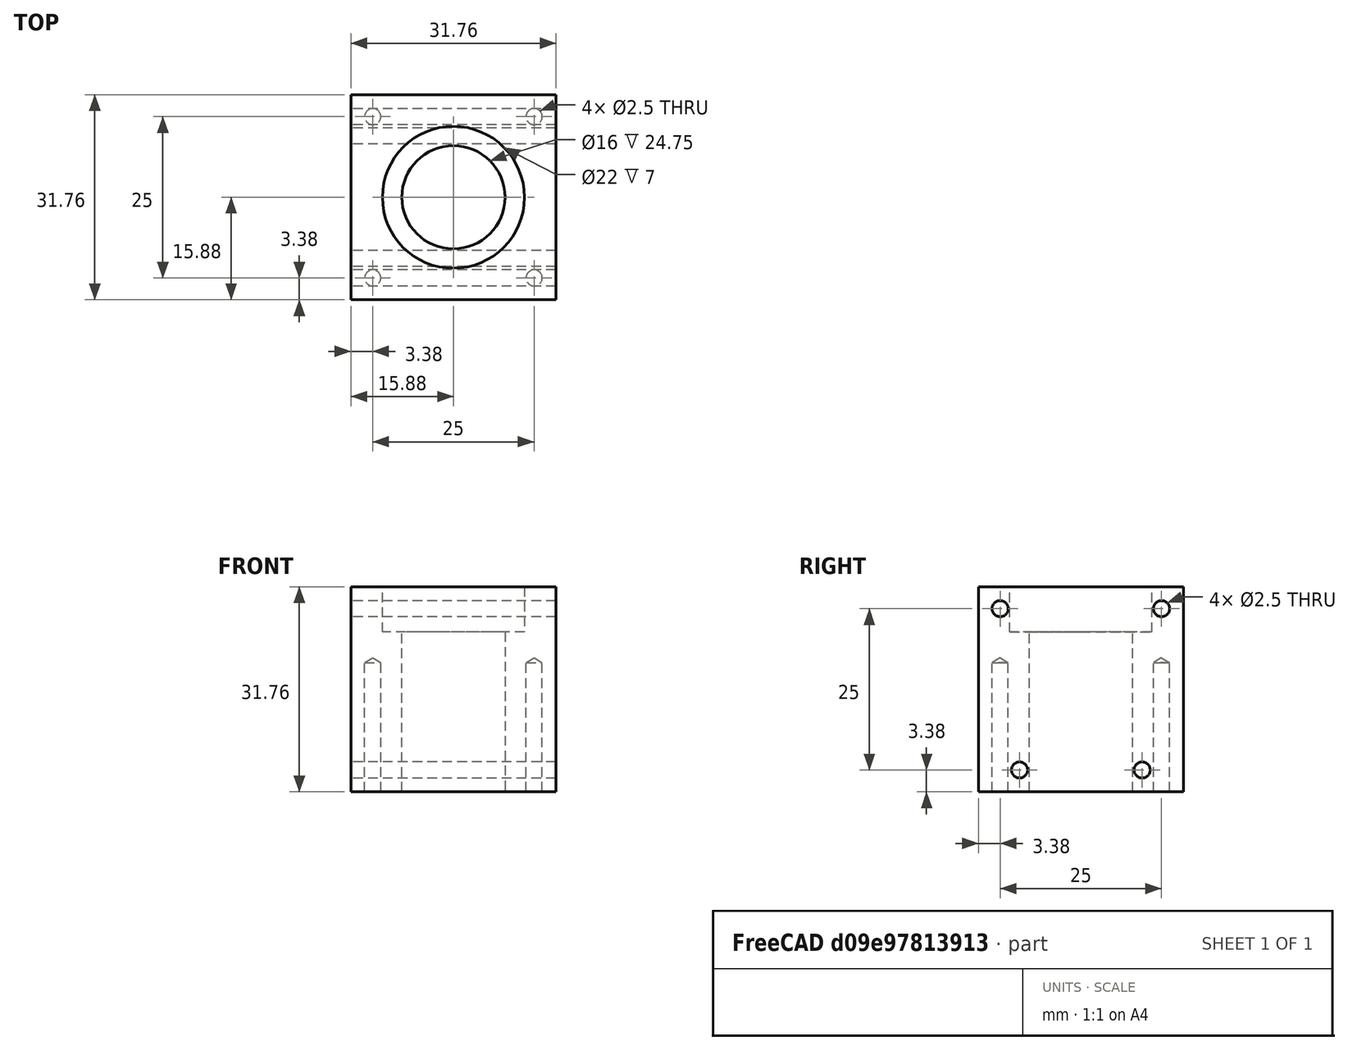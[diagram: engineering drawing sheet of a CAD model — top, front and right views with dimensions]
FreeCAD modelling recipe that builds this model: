
FCSTD DOCUMENT  (FreeCAD 0.21R33771 (Git))
Label: Upper Bearing Block
License: All rights reserved
LicenseURL: http://en.wikipedia.org/wiki/All_rights_reserved
objects: TechDraw::DrawViewDimension×8, Sketcher::SketchObject×5, TechDraw::DrawProjGroupItem×5, PartDesign::Pocket×2, PartDesign::Hole×2, TechDraw::DrawViewAnnotation×2, PartDesign::CoordinateSystem×2, TechDraw::DrawViewBalloon×2, PartDesign::Pad×1, TechDraw::DrawSVGTemplate×1, PartDesign::Body×1, TechDraw::DrawProjGroup×1, TechDraw::DrawPage×1
note: 18 computed .brp shape members not serialized (recipe doc carries the construction recipe); baked Part::Feature solids carry a one-line shape summary decoded from their .brp

FEATURE [Sketcher::SketchObject] Sketch
  FullyConstrained = true
  MapMode = 5
  Support = -> [XY_Plane]
  sketch-geometry (5):
    g0: LineSegment StartX=-15.875 StartY=-15.875 StartZ=0 EndX=-15.875 EndY=15.875 EndZ=0
    g1: LineSegment StartX=-15.875 StartY=15.875 StartZ=0 EndX=15.875 EndY=15.875 EndZ=0
    g2: LineSegment StartX=15.875 StartY=15.875 StartZ=0 EndX=15.875 EndY=-15.875 EndZ=0
    g3: LineSegment StartX=15.875 StartY=-15.875 StartZ=0 EndX=-15.875 EndY=-15.875 EndZ=0
    g4: GeomPoint X=0 Y=0 Z=0
  constraints (12):
    c: Coincident(g0,g1)
    c: Coincident(g1,g2)
    c: Coincident(g2,g3)
    c: Coincident(g3,g0)
    c: Horizontal(g1)
    c: Horizontal(g3)
    c: Vertical(g0)
    c: Vertical(g2)
    c: Symmetric(g1,g0,g4)
    c: Coincident(g4,g-1)
    c: DistanceY(g2,g2) = 31.75
    c: Equal(g2,g1)
FEATURE [PartDesign::Pad] Pad
  Direction = (0,0,1)
  Length = 31.75
  Length2 = 10
  Midplane = true
  Profile = -> Sketch
  ReferenceAxis = -> Sketch [N_Axis]
  Type = 0
FEATURE [Sketcher::SketchObject] Sketch001
  FullyConstrained = true
  MapMode = 5
  Placement = pos=(0,0,15.875) rot=(0,0,1;0rad)
  Support = -> [Pad]
  sketch-geometry (1):
    g0: Circle CenterX=0 CenterY=0 CenterZ=0 NormalX=0 NormalY=0 NormalZ=1 AngleXU=0 Radius=11
  constraints (2):
    c: Coincident(g0,g-1)
    c: Diameter(g0) = 22
FEATURE [PartDesign::Pocket] Pocket
  BaseFeature = -> Pad
  Direction = (1,1,1)
  Length = 7
  Length2 = 5
  Profile = -> Sketch001
  Type = 0
FEATURE [Sketcher::SketchObject] Sketch002
  FullyConstrained = true
  MapMode = 5
  Placement = pos=(0,0,19.05) rot=(0,0,1;0rad)
  sketch-geometry (1):
    g0: Circle CenterX=0 CenterY=0 CenterZ=0 NormalX=0 NormalY=0 NormalZ=1 AngleXU=0 Radius=8
  constraints (2):
    c: Coincident(g0,g-1)
    c: Diameter(g0) = 16
FEATURE [PartDesign::Pocket] Pocket001
  BaseFeature = -> Pocket
  Direction = (1,1,1)
  Length = 5
  Length2 = 5
  Profile = -> Sketch002
  Type = 1
FEATURE [Sketcher::SketchObject] Sketch003
  FullyConstrained = true
  MapMode = 5
  Placement = pos=(15.875,0,0) rot=(0.57735,0.57735,0.57735;2.0944rad)
  Support = -> [Pocket001]
  sketch-geometry (8):
    g0: Circle CenterX=-12.5 CenterY=12.5 CenterZ=0 NormalX=0 NormalY=0 NormalZ=1 AngleXU=0 Radius=1.25
    g1: Circle CenterX=12.5 CenterY=12.5 CenterZ=0 NormalX=0 NormalY=0 NormalZ=1 AngleXU=0 Radius=1.25
    g2: Circle CenterX=9.5 CenterY=-12.5 CenterZ=0 NormalX=0 NormalY=0 NormalZ=1 AngleXU=0 Radius=1.25
    g3: Circle CenterX=-9.5 CenterY=-12.5 CenterZ=0 NormalX=0 NormalY=0 NormalZ=1 AngleXU=0 Radius=1.25
    g4: LineSegment StartX=-12.5 StartY=12.5 StartZ=0 EndX=12.5 EndY=12.5 EndZ=0
    g5: LineSegment StartX=-9.5 StartY=-12.5 StartZ=0 EndX=9.5 EndY=-12.5 EndZ=0
    g6: GeomPoint X=0 Y=12.5 Z=0
    g7: GeomPoint X=0 Y=-12.5 Z=0
  constraints (17):
    c: Equal(g1,g0)
    c: Equal(g1,g3)
    c: Equal(g1,g2)
    c: Diameter(g1) = 2.5
    c: DistanceX(g3,g2) = 19
    c: Coincident(g4,g0)
    c: Coincident(g4,g1)
    c: Coincident(g5,g3)
    c: Coincident(g5,g2)
    c: Symmetric(g0,g1,g-2)
    c: Symmetric(g3,g2,g-2)
    c: PointOnObject(g6,g4)
    c: PointOnObject(g7,g5)
    c: PointOnObject(g7,g-2)
    c: Symmetric(g7,g6,g-1)
    c: DistanceX(g0,g1) = 25
    c: DistanceY(g7,g6) = 25
FEATURE [PartDesign::Hole] Hole
  BaseFeature = -> Pocket001
  CustomThreadClearance = 0
  Depth = 111.085
  DepthType = 1
  Diameter = 2.5
  DrillForDepth = false
  DrillPoint = 1
  DrillPointAngle = 118
  HoleCutCountersinkAngle = 90
  HoleCutCustomValues = false
  HoleCutDepth = 0
  HoleCutDiameter = 6.1
  HoleCutType = 0
  ModelThread = false
  Profile = -> Sketch003
  Tapered = false
  TaperedAngle = 90
  ThreadClass = 0
  ThreadDepth = 111.085
  ThreadDepthType = 0
  ThreadDirection = 0
  ThreadFit = 0
  ThreadSize = 9
  ThreadType = 1
  Threaded = true
  UseCustomThreadClearance = false
FEATURE [Sketcher::SketchObject] Sketch004
  FullyConstrained = true
  MapMode = 5
  Placement = pos=(0,0,-15.875) rot=(1,0,0;3.14159rad)
  Support = -> [Pocket001]
  sketch-geometry (9):
    g0: LineSegment StartX=-12.5 StartY=12.5 StartZ=0 EndX=-12.5 EndY=-12.5 EndZ=0
    g1: LineSegment StartX=-12.5 StartY=-12.5 StartZ=0 EndX=12.5 EndY=-12.5 EndZ=0
    g2: LineSegment StartX=12.5 StartY=-12.5 StartZ=0 EndX=12.5 EndY=12.5 EndZ=0
    g3: LineSegment StartX=12.5 StartY=12.5 StartZ=0 EndX=-12.5 EndY=12.5 EndZ=0
    g4: GeomPoint X=0 Y=0 Z=0
    g5: Circle CenterX=-12.5 CenterY=12.5 CenterZ=0 NormalX=0 NormalY=0 NormalZ=1 AngleXU=0 Radius=1.25
    g6: Circle CenterX=12.5 CenterY=12.5 CenterZ=0 NormalX=0 NormalY=0 NormalZ=1 AngleXU=0 Radius=1.25
    g7: Circle CenterX=12.5 CenterY=-12.5 CenterZ=0 NormalX=0 NormalY=0 NormalZ=1 AngleXU=0 Radius=1.25
    g8: Circle CenterX=-12.5 CenterY=-12.5 CenterZ=0 NormalX=0 NormalY=0 NormalZ=1 AngleXU=0 Radius=1.25
  constraints (20):
    c: Coincident(g0,g1)
    c: Coincident(g1,g2)
    c: Coincident(g2,g3)
    c: Coincident(g3,g0)
    c: Horizontal(g1)
    c: Horizontal(g3)
    c: Vertical(g0)
    c: Vertical(g2)
    c: Symmetric(g1,g0,g4)
    c: Coincident(g4,g-1)
    c: Equal(g3,g2)
    c: DistanceY(g2,g2) = 25
    c: Coincident(g5,g0)
    c: Coincident(g6,g2)
    c: Coincident(g7,g1)
    c: Coincident(g8,g0)
    c: Equal(g8,g7)
    c: Equal(g8,g6)
    c: Equal(g8,g5)
    c: Diameter(g8) = 2.5
FEATURE [PartDesign::Hole] Hole001
  BaseFeature = -> Hole
  CustomThreadClearance = 0
  Depth = 20
  DepthType = 0
  Diameter = 2.5
  DrillForDepth = false
  DrillPoint = 1
  DrillPointAngle = 118
  HoleCutCountersinkAngle = 90
  HoleCutCustomValues = false
  HoleCutDepth = 0
  HoleCutDiameter = 6.1
  HoleCutType = 0
  ModelThread = false
  Profile = -> Sketch004
  Tapered = false
  TaperedAngle = 90
  ThreadClass = 0
  ThreadDepth = 20
  ThreadDepthType = 0
  ThreadDirection = 0
  ThreadFit = 0
  ThreadSize = 9
  ThreadType = 1
  Threaded = true
  UseCustomThreadClearance = false
FEATURE [TechDraw::DrawSVGTemplate] Template
  EditableTexts = Designed_by_Name=RIO LIU; FC-Date=2022-12-13; FC-SC=1:1; FC-SH=2; FC-Title=UPPER BEARING BLOCK
  Height = 210
  Orientation = 1
  Width = 297
FEATURE [TechDraw::DrawViewAnnotation] Annotation
  Font = osifont
  LineSpace = 80
  LockPosition = false
  MaxWidth = -1
  Rotation = 0
  ScaleType = 0
  Text = ALL UNIT IN mm UNLESS SPECIFIED
  TextSize = 5
  TextStyle = 0
  X = 237.747
  Y = 136.46
FEATURE [TechDraw::DrawViewAnnotation] Annotation001
  Font = osifont
  LineSpace = 80
  LockPosition = false
  MaxWidth = -1
  Rotation = 0
  ScaleType = 0
  Text = ALL UNITS IN mm UNLESS SPECIFIED
  TextSize = 5
  TextStyle = 0
  X = 72.9226
  Y = 45.839
FEATURE [PartDesign::CoordinateSystem] Local_CS
  AttacherType = Attacher::AttachEngine3D
  MapMode = 45
  Placement = pos=(-1.8e-15,-2e-16,-3.5) rot=(0,0,1;0rad)
  Support = -> [Hole001]
FEATURE [PartDesign::CoordinateSystem] Local_CS001
  AttacherType = Attacher::AttachEngine3D
  MapMode = 11
  Placement = pos=(0,0,-15.875) rot=(0,0,1;1.5708rad)
  Support = -> [Hole001]
FEATURE [PartDesign::Body] Body  label="Upper Bearing Block"
  Group = -> [Sketch,Pad,Sketch001,Pocket,Sketch002,Pocket001,Sketch003,Hole,Sketch004,Hole001,Local_CS,Local_CS001]
  Origin = -> Origin
  Tip = -> Hole001
FEATURE [TechDraw::DrawProjGroupItem] ProjItem  label="Front"
  CoarseView = false
  Direction = (-1,0,-3e-16)
  Focus = 100
  HardHidden = true
  IsoCount = 0
  IsoHidden = false
  IsoVisible = false
  LockPosition = true
  Perspective = false
  Rotation = 0
  RotationVector = (1,0,0)
  ScaleType = 2
  ScrubCount = 0
  SeamHidden = false
  SeamVisible = true
  SmoothHidden = false
  SmoothVisible = true
  Source = -> [Body]
  Type = 0
  X = 0
  XDirection = (3e-16,1e-16,-1)
  Y = 0
FEATURE [TechDraw::DrawProjGroupItem] ProjItem005  label="FrontTopLeft"
  CoarseView = false
  Direction = (-0.57735,-0.57735,0.57735)
  Focus = 100
  HardHidden = false
  IsoCount = 0
  IsoHidden = false
  IsoVisible = false
  LockPosition = false
  Perspective = false
  Rotation = 0
  RotationVector = (1,0,0)
  ScaleType = 2
  ScrubCount = 0
  SeamHidden = false
  SeamVisible = true
  SmoothHidden = false
  SmoothVisible = true
  Source = -> [Body]
  Type = 6
  X = -63.3744
  XDirection = (-0.707107,1e-16,-0.707107)
  Y = 66.8475
FEATURE [TechDraw::DrawProjGroupItem] ProjItem006  label="FrontTopRight"
  CoarseView = false
  Direction = (-0.57735,-0.57735,-0.57735)
  Focus = 100
  HardHidden = false
  IsoCount = 0
  IsoHidden = false
  IsoVisible = false
  LockPosition = false
  Perspective = false
  Rotation = 0
  RotationVector = (1,0,0)
  ScaleType = 2
  ScrubCount = 0
  SeamHidden = false
  SeamVisible = true
  SmoothHidden = false
  SmoothVisible = true
  Source = -> [Body]
  Type = 7
  X = 63.3744
  XDirection = (0.707107,1e-16,-0.707107)
  Y = 66.8475
FEATURE [TechDraw::DrawProjGroupItem] ProjItem007  label="Right"
  CoarseView = false
  Direction = (2e-16,1e-16,-1)
  Focus = 100
  HardHidden = false
  IsoCount = 0
  IsoHidden = false
  IsoVisible = false
  LockPosition = false
  Perspective = false
  Rotation = 0
  RotationVector = (1,0,0)
  ScaleType = 2
  ScrubCount = 0
  SeamHidden = false
  SeamVisible = true
  SmoothHidden = false
  SmoothVisible = true
  Source = -> [Body]
  Type = 2
  X = 56.7988
  XDirection = (1,0,2e-16)
  Y = 0
FEATURE [TechDraw::DrawProjGroupItem] ProjItem008  label="Left"
  CoarseView = false
  Direction = (-4e-16,-1e-16,1)
  Focus = 100
  HardHidden = false
  IsoCount = 0
  IsoHidden = false
  IsoVisible = false
  LockPosition = false
  Perspective = false
  Rotation = 0
  RotationVector = (1,0,0)
  ScaleType = 2
  ScrubCount = 0
  SeamHidden = false
  SeamVisible = true
  SmoothHidden = false
  SmoothVisible = true
  Source = -> [Body]
  Type = 1
  X = -76.2517
  XDirection = (-1,0,-4e-16)
  Y = 0
FEATURE [TechDraw::DrawProjGroup] ProjGroup
  Anchor = -> ProjItem
  AutoDistribute = false
  LockPosition = false
  ProjectionType = 1
  Rotation = 0
  ScaleType = 0
  Source = -> [Body]
  Views = -> [ProjItem,ProjItem005,ProjItem006,ProjItem007,ProjItem008]
  X = 141.95
  Y = 94.6369
  spacingX = 15
  spacingY = 15
FEATURE [TechDraw::DrawViewDimension] Dimension
  AngleOverride = false
  Arbitrary = false
  ArbitraryTolerances = false
  EqualTolerance = true
  ExtensionAngle = 0
  FormatSpec = ⌀%.2w
  FormatSpecOverTolerance = %+.2w
  FormatSpecUnderTolerance = %+.2w
  Inverted = false
  LineAngle = 0
  LockPosition = false
  MeasureType = 1
  OverTolerance = 0
  References2D = -> [ProjItem008]
  Rotation = 0
  ScaleType = 0
  TheoreticalExact = false
  Type = 5
  UnderTolerance = 0
  X = 23.9852
  Y = 21.3821
FEATURE [TechDraw::DrawViewDimension] Dimension001
  AngleOverride = false
  Arbitrary = false
  ArbitraryTolerances = false
  EqualTolerance = true
  ExtensionAngle = 0
  FormatSpec = ⌀%.2w
  FormatSpecOverTolerance = %+.2w
  FormatSpecUnderTolerance = %+.2w
  Inverted = false
  LineAngle = 0
  LockPosition = false
  MeasureType = 1
  OverTolerance = 0
  References2D = -> [ProjItem008]
  Rotation = 0
  ScaleType = 0
  TheoreticalExact = false
  Type = 5
  UnderTolerance = 0
  X = 23.9852
  Y = 12.6433
FEATURE [TechDraw::DrawViewBalloon] Balloon
  BubbleShape = 1
  EndType = 0
  EndTypeScale = 1
  KinkLength = 5
  LockPosition = false
  OriginX = -11.25
  OriginY = 12.5
  Rotation = 0
  ScaleType = 0
  ShapeScale = 1
  SourceView = -> ProjItem007
  Text = M3 ↓20 TYP
  TextWrapLen = -1
  X = 21.3101
  Y = 27.9172
FEATURE [TechDraw::DrawViewBalloon] Balloon001
  BubbleShape = 1
  EndType = 0
  EndTypeScale = 1
  KinkLength = 5
  LockPosition = false
  OriginX = -13.7365
  OriginY = 12.5
  Rotation = 0
  ScaleType = 0
  ShapeScale = 1
  SourceView = -> ProjItem
  Text = M3 THRU TYP
  TextWrapLen = -1
  X = 34.8845
  Y = 27.8669
FEATURE [TechDraw::DrawViewDimension] Dimension005
  AngleOverride = false
  Arbitrary = false
  ArbitraryTolerances = false
  EqualTolerance = true
  ExtensionAngle = 0
  FormatSpec = %.2w
  FormatSpecOverTolerance = %+.2w
  FormatSpecUnderTolerance = %+.2w
  Inverted = false
  LineAngle = 0
  LockPosition = false
  MeasureType = 1
  OverTolerance = 0
  References2D = -> [ProjItem]
  Rotation = 0
  ScaleType = 0
  TheoreticalExact = false
  Type = 1
  UnderTolerance = 0
  X = -25.7954
  Y = -15.4227
FEATURE [TechDraw::DrawViewDimension] Dimension008
  AngleOverride = false
  Arbitrary = false
  ArbitraryTolerances = false
  EqualTolerance = true
  ExtensionAngle = 0
  FormatSpec = %.1f
  FormatSpecOverTolerance = %+.1f
  FormatSpecUnderTolerance = %+.1f
  Inverted = false
  LineAngle = 0
  LockPosition = false
  MeasureType = 1
  OverTolerance = 0
  References2D = -> [ProjItem]
  Rotation = 0
  ScaleType = 0
  TheoreticalExact = false
  Type = 2
  UnderTolerance = 0
  X = -37.8217
  Y = 26.5094
FEATURE [TechDraw::DrawViewDimension] Dimension009
  AngleOverride = false
  Arbitrary = false
  ArbitraryTolerances = false
  EqualTolerance = true
  ExtensionAngle = 0
  FormatSpec = %.1f
  FormatSpecOverTolerance = %+.1f
  FormatSpecUnderTolerance = %+.1f
  Inverted = false
  LineAngle = 0
  LockPosition = false
  MeasureType = 1
  OverTolerance = 0
  References2D = -> [ProjItem]
  Rotation = 0
  ScaleType = 0
  TheoreticalExact = false
  Type = 2
  UnderTolerance = 0
  X = -28.785
  Y = 26.6746
FEATURE [TechDraw::DrawViewDimension] Dimension011
  AngleOverride = false
  Arbitrary = false
  ArbitraryTolerances = false
  EqualTolerance = true
  ExtensionAngle = 0
  FormatSpec = %.1f
  FormatSpecOverTolerance = %+.1f
  FormatSpecUnderTolerance = %+.1f
  Inverted = false
  LineAngle = 0
  LockPosition = false
  MeasureType = 1
  OverTolerance = 0
  References2D = -> [ProjItem007]
  Rotation = 0
  ScaleType = 0
  TheoreticalExact = false
  Type = 2
  UnderTolerance = 0
  X = 28.0824
  Y = -3.88621
FEATURE [TechDraw::DrawViewDimension] Dimension012
  AngleOverride = false
  Arbitrary = false
  ArbitraryTolerances = false
  EqualTolerance = true
  ExtensionAngle = 0
  FormatSpec = %.1f
  FormatSpecOverTolerance = %+.1f
  FormatSpecUnderTolerance = %+.1f
  Inverted = false
  LineAngle = 0
  LockPosition = false
  MeasureType = 1
  OverTolerance = 0
  References2D = -> [ProjItem007]
  Rotation = 0
  ScaleType = 0
  TheoreticalExact = false
  Type = 1
  UnderTolerance = 0
  X = 22.9747
  Y = -19.893
FEATURE [TechDraw::DrawViewDimension] Dimension013
  AngleOverride = false
  Arbitrary = false
  ArbitraryTolerances = false
  EqualTolerance = true
  ExtensionAngle = 0
  FormatSpec = %.1f
  FormatSpecOverTolerance = %+.1f
  FormatSpecUnderTolerance = %+.1f
  Inverted = false
  LineAngle = 0
  LockPosition = false
  MeasureType = 1
  OverTolerance = 0
  References2D = -> [ProjItem]
  Rotation = 0
  ScaleType = 0
  TheoreticalExact = false
  Type = 1
  UnderTolerance = 0
  X = -11.74
  Y = 36.2422
FEATURE [TechDraw::DrawPage] Page
  KeepUpdated = true
  NextBalloonIndex = 3
  ProjectionType = 0
  Template = -> Template
  Views = -> [ProjGroup,Dimension,Dimension001,Balloon,Balloon001,Dimension005,Annotation001,Dimension008,Dimension009,Dimension011,Dimension012,Dimension013]
